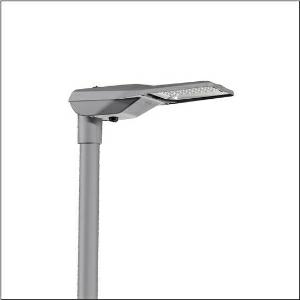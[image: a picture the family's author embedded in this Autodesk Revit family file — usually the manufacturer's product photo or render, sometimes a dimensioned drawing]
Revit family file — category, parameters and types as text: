
# Revit family: streetlight_sl_21_mini___st0_8a_5xe2c43t08hb_23df
name_source: partatom
category: Lighting Fixtures
units: mm (PartAtom-declared; Revit-internal decimal feet)

## family parameters
Cut with Voids When Loaded = No
Host = Face
Light Source = No
Part Type = Normal
Room Calculation Point = No
Round Connector Dimension = Use Diameter
Shared = No

## types (1)
- --- (1 x LED, 9430 lm, 66 W, 4000K)
    Apparent Load = 66 VA
    CIE Flux Codes = 38 75 97 100 100
    Color Rendering = 70
    Color Temperature = 4000K
    Default Elevation = 1800 mm
    Description = Streetlight SL 21 mini, mast luminaire, primary light control with lens, of PMMA, primary optical cover: cover, of toughened safety glass, transparent, light distribution: ST0.8a, light emission: direct distribution, primary light characteristic: asymmetric, installation type: side-entry, post-top, LED, High Power LED, rated luminous flux: 9.430lm, luminous efficacy: 143lm/W, light colour: 740, colour temperature: 4000K, control gear: D4i, control: overheat protection, constant luminous flux control, time-dependent luminous flux control, flexible luminous flux parameterisation, pre-setting: logarithmic dimming characteristic, mains connection: 220..240V, AC, 50/60Hz, start of lifetime: 66W, end of service life: 69W, reduction: 30W, luminaire housing, of diecast aluminium, powder-coated, Siteco® metallic grey (DB 702S), corrosivity category C5 mid according to DIN EN ISO 12944, please order mast flange separately, inclination adjustable: 0°, 5°, 10°, 15°, sealing non-destructively replaceable, multi-level sealing system, length: 628mm, width: 235mm, height: 110mm, mast flange for spigot size: 42mm (side-entry): 5XC10008XM4, 60/48mm (side-entry/post-top): 5XC10108XM2, 76/60mm (side-entry/post-top): 5XC10108XM1, mounting height: 4..8m, Smart Interface below and above, protection rating (complete): IP66, insulation class (complete): insulation class II (safety insulation), certification: CE, ENEC, ENEC+, VDE, impact resistance: IK10, permissible operating ambient temperature for outdoor applications: -40..+50°C, standard-compliant lighting for roads and squares, packaging unit: 1 piece

Light Distribution: ST0.8a
    Height = 110 mm
    Lamp = 1 x LED
    Lamp Light Flux = 9430 lm
    Lamp Power = 66 W
    Lamp count = 1
    Length = 625 mm
    Luminous efficacy = 143 lm/W
    Manufacturer = Siteco
    ModVariant = No
    Model = 5XE2C43T08HB
    Number of Poles = 1
    OnlyDefault = Yes
    Power Factor = 1
    Product Name = Streetlight SL 21 mini | ST0.8a
    Product group = mast luminaire | pylon top
    ProductGroupID = 6100
    Protection Class = Protection class II
    Protection Degree = IP 66
    RLX_Detail_Level = 1
    RLX_Emergency_Light_Flux = 0 lm
    RLX_Emergency_Type = 0
    RLX_Emergency_Type_DB = No
    RlxData = <blob elided: 26329 chars, md5=47ce39c1>
    Socket = socket
    Standby Power = 0 W
    System Light Flux = 9430 lm
    System Power = 66 W
    Type Comments = factory setting: luminous flux: 100 % | dim-lin: 254 | 670 mA
    Type Image = l_1003514.jpg
    URL = http://relux.com
    VarID = @adj_206571
    Voltage = 0 V
    Weight = 0.00 kg
    Width = 234 mm

## geometry (parser evidence)
native form markers: Blend x4, Sweep x12
no freeform markers — native parametric forms only
